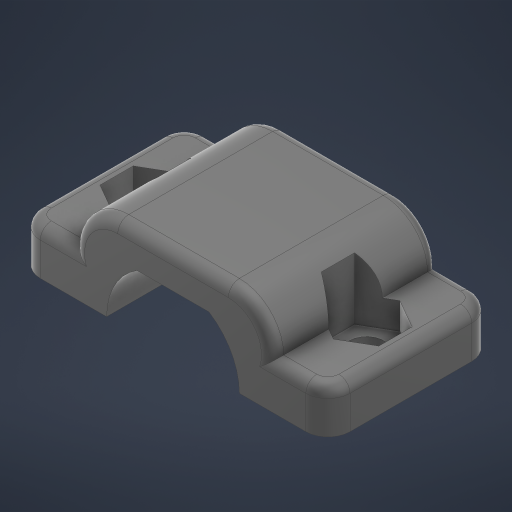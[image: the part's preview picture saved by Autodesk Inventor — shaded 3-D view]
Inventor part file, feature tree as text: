
AUTODESK INVENTOR PART (.ipt)
format: ipt  version: 2024 (Build 280153000, 153)  size: 343,552 bytes
history: native  units: in
note: dims shown in document units (in); Inventor stores cm internally (conversion verified against a paired STEP export)
features: sketch x3, extrude x2, plane x2, fillet x2, hole x1, mirror x1
ambient origin geometry x8: Origin, YZ Plane, XZ Plane, XY Plane, X Axis, Y Axis, Z Axis, Center Point
bodies: Solid1 (feature_tree)
feature tree (11):
  extrude  "Extrusion2"  Depth=0.1181in TaperAngle=0.0deg
  plane  "Work Plane1"
  extrude  "Extrusion3"  Depth=0.1575in
  hole  "Hole1"  [1 undecoded]
  mirror  "Mirror1"
  plane  "Work Plane2"
  fillet  "Fillet3"  Radius=0.2953in
  fillet  "Fillet4"  Radius=0.0787in
  sketch  "Sketch3"  dims[d20=0.1575in d21=0.1969in d22=0.315in d23=0.1181in d24=0.5906in d25=0.0in]
  sketch  "Sketch4"  dims[d26=0.2366in d27=0.1575in]
  sketch  "Sketch5"  dims[d28=0.315in d29=0.0945in d30=0.0in d31=0.0in d32=0.122in d33=0.2362in d34=0.1575in d35=0.0787in d36=90.0deg d37=0.315in d38=0.8108in d39=0.2953in d40=0.2953in d42=0.0787in d43=0.0394in]
note: 1 required parameter value undecoded (feature->parameter linkage not recoverable at this tier; creation-order binding heuristic only, values carry confidence <= 0.55)
